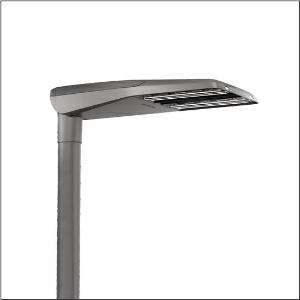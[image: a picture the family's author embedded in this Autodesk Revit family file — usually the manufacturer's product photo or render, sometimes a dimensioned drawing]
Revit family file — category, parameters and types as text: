
# Revit family: streetlight_sl_11_iq_midi___st1_0p1_0_5xc3k51g08me_2a46
name_source: partatom
category: Lighting Fixtures
units: mm (PartAtom-declared; Revit-internal decimal feet)

## family parameters
Cut with Voids When Loaded = No
Host = Face
Light Source = No
Part Type = Normal
Room Calculation Point = No
Round Connector Dimension = Use Diameter
Shared = No

## types (1)
- --- (1 x LED, 9410 lm, 63 W, 3000K)
    Apparent Load = 63 VA
    CIE Flux Codes = 32 65 95 100 100
    Color Rendering = 70
    Color Temperature = 3000K
    Default Elevation = 1800 mm
    Description = Streetlight SL 11 iQ midi, mast luminaire, primary light control with 3 zone facetted reflector, of plastic, silver coated, highly specular, primary optical cover: cover, of PMMA, transparent, light distribution: ST1.0P1.0, light emission: direct distribution, primary light characteristic: asymmetric, installation type: post-top, side-entry, LED, High Power LED, rated luminous flux: 9.410lm, luminous efficacy: 149lm/W, light colour: 730, colour temperature: 3000K, control: Street-Remote, Auto-Match, Temp-Guard, Lumen-Switch, Night-Set, Smart-Wire, Light-Fading, Desk-Remote (wireless, voltage-free reading and setting of iQ features in the workshop via application-optimized NFC function/RFID function), optimised constant luminous flux control (CLO 2.0), presetting dimming linear, with cable H07RN-F 5x 1.5mm², mains connection: 230..240V, AC, 50/60Hz, connection cable pre-assembled, cable length: 12,5m, start of lifetime: 63W, end of service life: 67W, reduction: 30W, luminaire housing, of diecast aluminium, powder-coated, Siteco® metallic grey (DB 702S), please order mast flange separately, inclination adjustable without tools: 0°, 5°, 10°, 15° (post-top) | 0°, -5°, -10°, -15° (side-entry), sealing non-destructively replaceable, multi-level sealing system, length: 780mm, width: 376mm, height: 118mm, mast flange for spigot size: 42mm (side-entry): 5XC10008XM4, 60/48mm (side-entry/post-top): 5XC10108XM2, 76/60mm (side-entry/post-top): 5XC10108XM1, equipment: Power, protection rating (complete): IP66, insulation class (complete): insulation class II (safety insulation), certification: CE, ENEC, VDE, impact resistance: IK09, permissible operating ambient temperature for outdoor applications: -25..+50°C, standard-compliant lighting for roads and squares, Environmental Product Declaration (EPD) tested and certified by an independent institute, packaging unit: 1 piece

Light Distribution: ST1.0P1.0
    Height = 118 mm
    Lamp = 1 x LED
    Lamp Light Flux = 9410 lm
    Lamp Power = 63 W
    Lamp count = 1
    Length = 780 mm
    Luminous efficacy = 149 lm/W
    Manufacturer = Siteco
    ModVariant = No
    Model = 5XC3K51G08ME
    Number of Poles = 1
    OnlyDefault = Yes
    Power Factor = 1
    Product Name = Streetlight SL 11 iQ midi | ST1.0P1.0
    Product group = mast luminaire | pylon top
    ProductGroupID = 6100
    Protection Class = Protection class II
    Protection Degree = IP 66
    RLX_Detail_Level = 1
    RLX_Emergency_Light_Flux = 0 lm
    RLX_Emergency_Type = 0
    RLX_Emergency_Type_DB = No
    RlxData = <blob elided: 70589 chars, md5=ec15e9f8>
    Socket = socket
    Standby Power = 0 W
    System Light Flux = 9410 lm
    System Power = 63 W
    Type Comments = factory setting: luminous flux: 100 % | dim-lin: 254 | 553 mA
    Type Image = l_1005960.jpg
    URL = http://relux.com
    VarID = @adj_021539
    Voltage = 0 V
    Weight = 0.00 kg
    Width = 376 mm

## geometry (parser evidence)
native form markers: Blend x4, Sweep x8
no freeform markers — native parametric forms only
